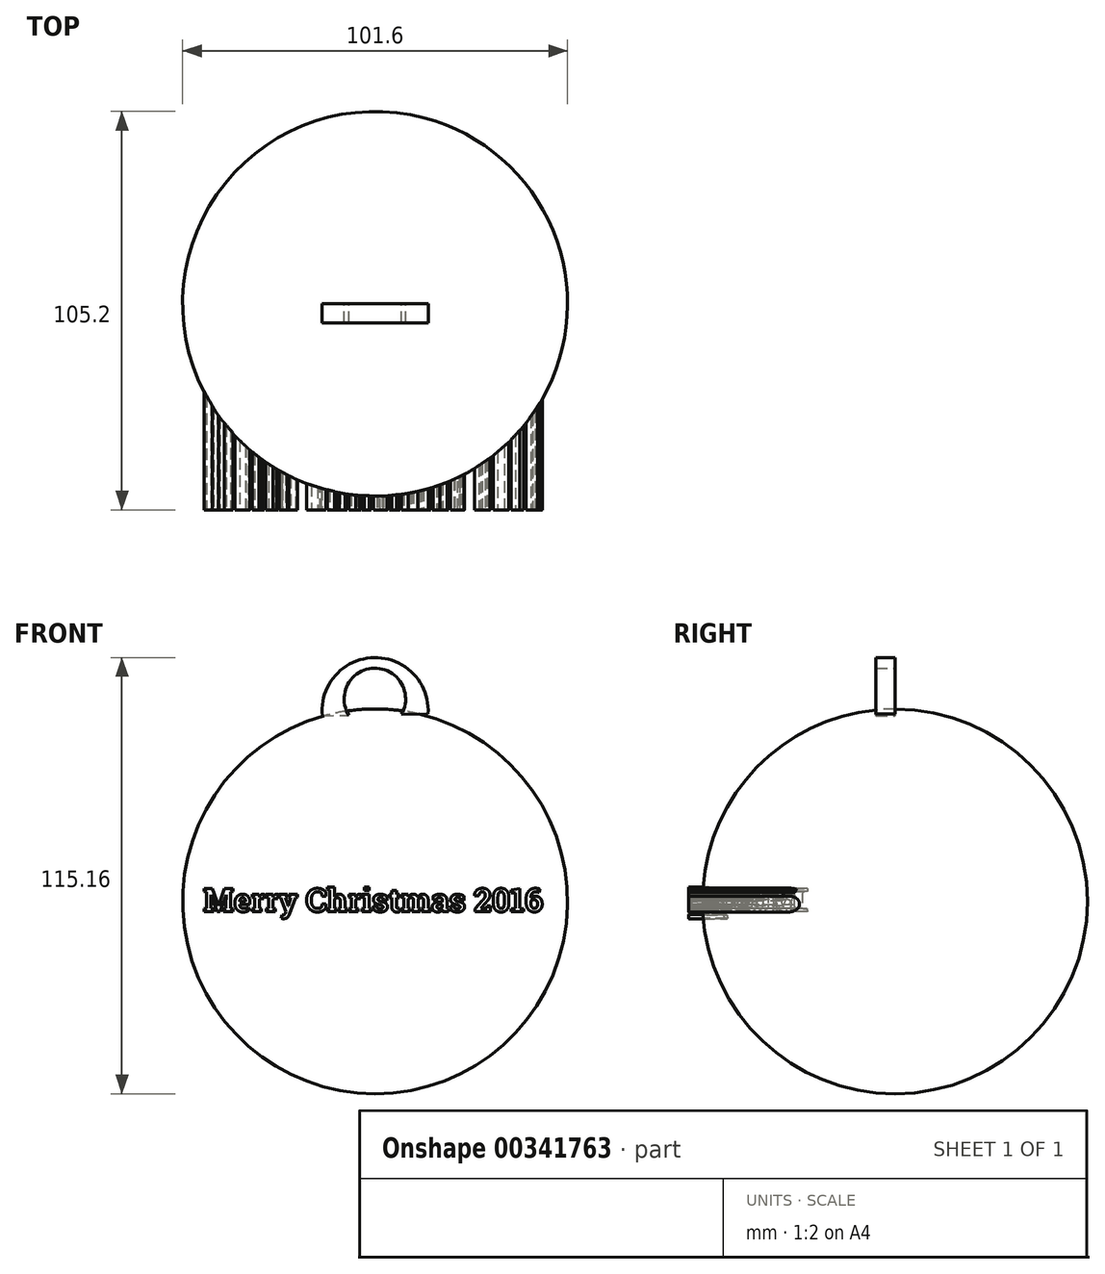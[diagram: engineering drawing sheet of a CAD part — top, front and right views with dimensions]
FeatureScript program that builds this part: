
annotation { "Feature Type Name" : "Feature", "Feature Type Description" : "" }
export const myFeature = defineFeature(function(context is Context, id is Id, definition is map)
    precondition{}
    {
        {
            var Q0;
            Q0=qCreatedBy(makeId("Front.planeOp"),FACE);
            var sketch = newSketch(context, id + "F0", { "sketchPlane" : qUnion([Q0])});
            skArc(sketch, "E0", {"start": v(0, -50.8) * mm, "mid": v(50.8, 0) * mm, "end": v(0, 50.8) * mm});
            skLineSegment(sketch, "E1", {"start": v(0, 50.8) * mm, "end": v(0, -50.8) * mm});
            skSolve(sketch);
        }
        {
            var Q0;
            Q0=makeQuery(id+"F0.imprint","IMPRINT",FACE,{"disambiguationData":[TD([[makeQuery(id+"F0.imprint","IMPRINT",EDGE,{"derivedFrom":sQuery(id+"F0.wireOp",EDGE,"E0")}),1.0]])]});
            var Q1;
            Q1=sQuery(id+"F0.wireOp",EDGE,"E1");
            revolve(context, id + "F1", {"entities" : qUnion([Q0]), "axis" : qUnion([Q1]), "revolveType" : RevolveType.FULL});
        }
        {
            var Q0;
            Q0=qCreatedBy(makeId("Front.planeOp"),FACE);
            var sketch = newSketch(context, id + "F2", { "sketchPlane" : qUnion([Q0])});
            skArc(sketch, "E2", {"start": v(13.98, 49.53) * mm, "mid": v(-0.27, 64.36) * mm, "end": v(-13.94, 48.98) * mm});
            skLineSegment(sketch, "E3", {"start": v(-13.94, 48.98) * mm, "end": v(13.98, 49.53) * mm});
            skArc(sketch, "E4", {"start": v(6.98, 49.39) * mm, "mid": v(-0.22, 61.55) * mm, "end": v(-6.94, 49.12) * mm});
            skSolve(sketch);
        }
        {
            var Q0;
            Q0=makeQuery(id+"F2.imprint","IMPRINT",FACE,{"disambiguationData":[TD([[makeQuery(id+"F2.imprint","IMPRINT",EDGE,{"derivedFrom":sQuery(id+"F2.wireOp",EDGE,"E2")}),1.0]])]});
            var Q1;
            Q1=makeQuery(id+"FdCqvT0ZURC80FY_1.opExtrude","CAP_FACE",FACE,{"disambiguationData":[OSD([sQuery(id+"F2.wireOp",EDGE,"E2"),sQuery(id+"F2.wireOp",EDGE,"E3")])],"isStart":false});
            extrude(context, id + "F3", {"entities" : qUnion([Q0, Q1]), "depth" : 5 * mm});
        }
        {
            var Q0;
            Q0=qCreatedBy(makeId("Front.planeOp"),FACE);
            cPlane(context, id + "F4", {"entities" : qUnion([Q0]), "cplaneType" : CPlaneType.OFFSET, "offset" : 54.4 * mm, "width" : 150 * mm, "height" : 150 * mm});
        }
        {
            var Q0;
            Q0=qCreatedBy(id+"F4.planeOp",FACE);
            var sketch = newSketch(context, id + "F5", { "sketchPlane" : qUnion([Q0])});
            skText(sketch, "E5", { "text": "Merry Christmas 2016", "fontName": "RobotoSlab-Bold.ttf"});
            const initialGuessF5  = {"E5": [-0.0454, -0.00274, 1, 0, 0.00619]};
            skSetInitialGuess(sketch, initialGuessF5);
            skSolve(sketch);
        }
        {
            var Q0;
            Q0 = qSketchRegion(id + "F5", true);
            extrude(context, id + "F6", {"entities" : qUnion([Q0]), "operationType" : NewBodyOperationType.ADD, "endBound" : BoundingType.UP_TO_NEXT, "oppositeDirection" : true, "depth" : 25 * mm});
        }
    });
